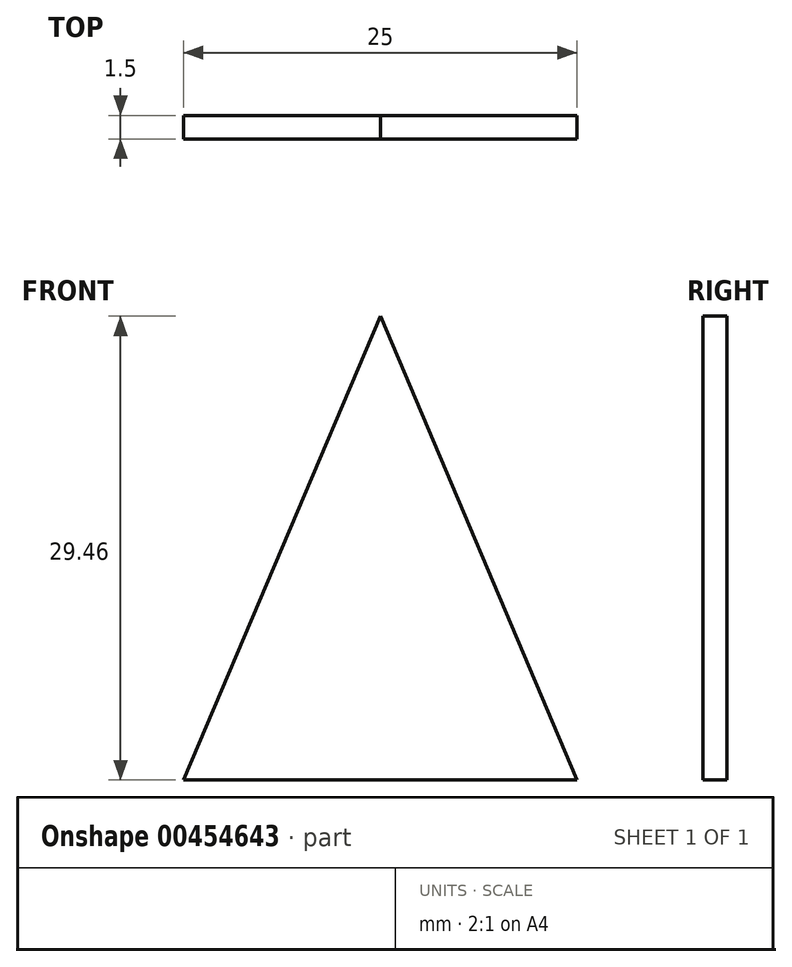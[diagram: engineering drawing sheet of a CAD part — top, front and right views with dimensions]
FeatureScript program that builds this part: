
annotation { "Feature Type Name" : "Feature", "Feature Type Description" : "" }
export const myFeature = defineFeature(function(context is Context, id is Id, definition is map)
    precondition{}
    {
        {
            var Q0;
            Q0=qCreatedBy(makeId("Front.planeOp"),FACE);
            var sketch = newSketch(context, id + "F0", { "sketchPlane" : qUnion([Q0])});
            skLineSegment(sketch, "E0", {"start": v(-12.5, 0) * mm, "end": v(12.5, 0) * mm});
            skLineSegment(sketch, "E1", {"start": v(12.5, 0) * mm, "end": v(0, 29.46) * mm});
            skLineSegment(sketch, "E2", {"start": v(0, 29.46) * mm, "end": v(-12.5, 0) * mm});
            skSolve(sketch);
        }
        {
            var Q0;
            Q0 = qSketchRegion(id + "F0", true);
            extrude(context, id + "F1", {"entities" : qUnion([Q0]), "depth" : 1.5 * mm, "offsetDistance" : 25 * mm});
        }
    });
